# Revit family: BSK_NOTUS HV_VERTICAL_LOD400
name_source: partatom
category: Mechanical Equipment
units: mm (PartAtom-declared; Revit-internal decimal feet)

## family parameters
Always vertical = Yes
Cut with Voids When Loaded = No
Maintain Annotation Orientation = No
OmniClass Number = 23.75.00.00
OmniClass Title = Climate Control (HVAC)
Part Type = Normal
Room Calculation Point = No
Round Connector Dimension = Use Diameter
Shared = No
Work Plane-Based = No

## types (2) — shared parameters
Cap Material = Aluminum 3003-H12
Clearence = 500 mm  [stored 1.64042 ft]
Coef_a = -0.000464
Coef_b = -0.539786
Coef_c = 434.9
Depth = 550 mm
Height = 800 mm  [stored 2.62467 ft]
Manufacturer = BSK Havalandırma Ekipmanları AŞ
Max Electrical Power = 150 W
Max. Flow Rate (@100 Pa) = 375 m3/h
Max. Thermal Efficiency = 92%
Model = Notus
Operating Temperature = -25 / +50
SEC Class = A+
Supply Frequency = 50/60Hz
Supply Voltage = 230 V
Unit_Flow = 1.0 CMH
Unit_Press = 1.0 Pa
Website = www.bskhvac.com.tr
Weight = 18kg
Width = 500 mm  [stored 1.64042 ft]
zero-valued in all types: Default Elevation

## per-type parameters (varying)
| type | BSK_Air Outlets Bottom | BSK_Air Outlets Top | Casing Material |
| TYPE 1 (TOP) | No | Yes | Aluminum |
| TYPE 2 (BOTTOM) | Yes | No | Aluminium |

note: [stored X ft] marks values corroborated as IEEE doubles in the binary element streams (Revit-internal decimal feet)

## geometry (parser evidence)
native form markers: Sweep x3
no freeform markers — native parametric forms only
